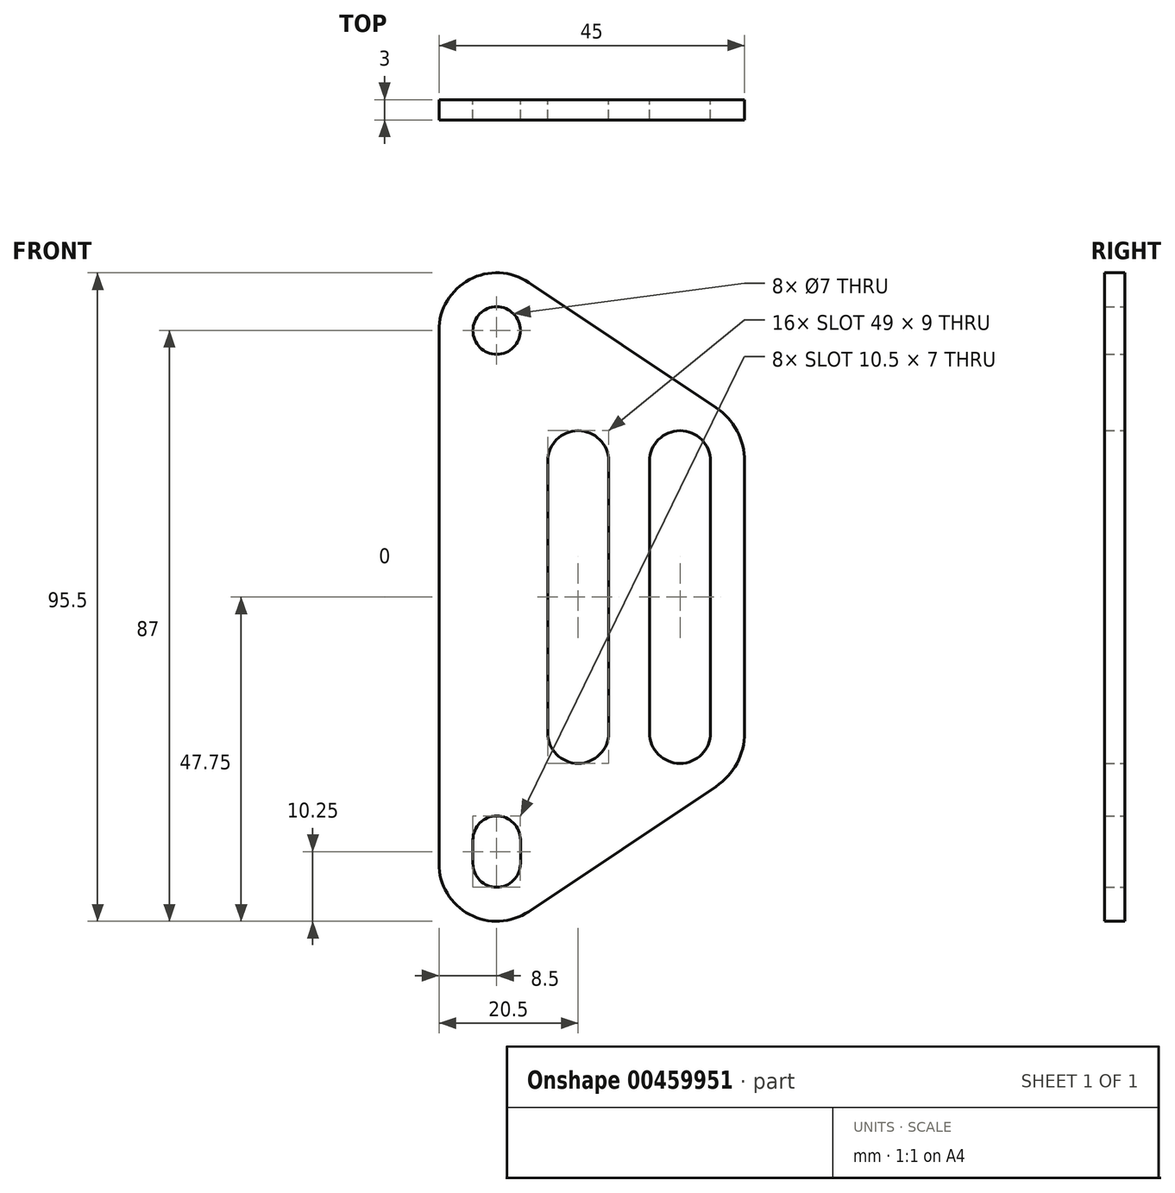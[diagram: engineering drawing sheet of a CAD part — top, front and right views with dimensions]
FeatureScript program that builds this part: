
annotation { "Feature Type Name" : "Feature", "Feature Type Description" : "" }
export const myFeature = defineFeature(function(context is Context, id is Id, definition is map)
    precondition{}
    {
        {
            var Q0;
            Q0=qCreatedBy(makeId("Front.planeOp"),FACE);
            var sketch = newSketch(context, id + "F0", { "sketchPlane" : qUnion([Q0])});
            skCircle(sketch, "E0", {"center": v(0, 0) * mm, "radius": 3.5 * mm});
            skArc(sketch, "E1", {"start": v(3.5, -75) * mm, "mid": v(0, -71.5) * mm, "end": v(-3.5, -75) * mm});
            skArc(sketch, "E2", {"start": v(-3.5, -78.5) * mm, "mid": v(0, -82) * mm, "end": v(3.5, -78.5) * mm});
            skLineSegment(sketch, "E3", {"start": v(3.5, -75) * mm, "end": v(3.5, -78.5) * mm});
            skLineSegment(sketch, "E4", {"start": v(-3.5, -75) * mm, "end": v(-3.5, -78.5) * mm});
            skArc(sketch, "E5.0", {"start": v(4.72, 7.07) * mm, "mid": v(-4, 7.5) * mm, "end": v(-8.5, 0) * mm});
            skLineSegment(sketch, "E6", {"start": v(-8.5, 0) * mm, "end": v(-8.5, -78.5) * mm});
            skArc(sketch, "E7.0", {"start": v(-8.5, -78.5) * mm, "mid": v(-4, -86) * mm, "end": v(4.72, -85.57) * mm});
            skLineSegment(sketch, "E8.0", {"start": v(36.5, -19.25) * mm, "end": v(36.5, -59.25) * mm});
            skLineSegment(sketch, "E9.0", {"start": v(27, 0) * mm, "end": v(27, -78.5) * mm, "construction": true});
            skPoint(sketch, "E10.endSnap0", {"position": v(36.5, -39.25) * mm});
            skArc(sketch, "E11", {"start": v(31.5, -19.25) * mm, "mid": v(27, -14.75) * mm, "end": v(22.5, -19.25) * mm});
            skArc(sketch, "E12", {"start": v(22.5, -59.25) * mm, "mid": v(27, -63.75) * mm, "end": v(31.5, -59.25) * mm});
            skArc(sketch, "E13", {"start": v(36.5, -19.25) * mm, "mid": v(35.38, -14.77) * mm, "end": v(32.28, -11.35) * mm});
            skArc(sketch, "E14", {"start": v(32.28, -67.15) * mm, "mid": v(35.38, -63.73) * mm, "end": v(36.5, -59.25) * mm});
            skLineSegment(sketch, "E15", {"start": v(4.72, 7.07) * mm, "end": v(32.28, -11.35) * mm});
            skLineSegment(sketch, "E16", {"start": v(32.28, -67.15) * mm, "end": v(4.72, -85.57) * mm});
            skLineSegment(sketch, "E17", {"start": v(22.5, -19.25) * mm, "end": v(22.5, -59.25) * mm});
            skLineSegment(sketch, "E18", {"start": v(31.5, -19.25) * mm, "end": v(31.5, -59.25) * mm});
            skPoint(sketch, "E19.orphan", {"position": v(36.5, 0) * mm});
            skPoint(sketch, "E20.orphan", {"position": v(36.5, -78.5) * mm});
            skArc(sketch, "E21.1.0.0", {"start": v(16.5, -19.25) * mm, "mid": v(12, -14.75) * mm, "end": v(7.5, -19.25) * mm});
            skLineSegment(sketch, "E21.1.0.1", {"start": v(7.5, -19.25) * mm, "end": v(7.5, -59.25) * mm});
            skLineSegment(sketch, "E21.1.0.2", {"start": v(16.5, -19.25) * mm, "end": v(16.5, -59.25) * mm});
            skArc(sketch, "E21.1.0.3", {"start": v(7.5, -59.25) * mm, "mid": v(12, -63.75) * mm, "end": v(16.5, -59.25) * mm});
            skLineSegment(sketch, "E21.direction1", {"start": v(22.5, -59.25) * mm, "end": v(7.5, -59.25) * mm, "construction": true});
            skSolve(sketch);
        }
        {
            var Q0;
            Q0 = qSketchRegion(id + "F0", true);
            extrude(context, id + "F1", {"entities" : qUnion([Q0]), "depth" : 3 * mm});
        }
    });
